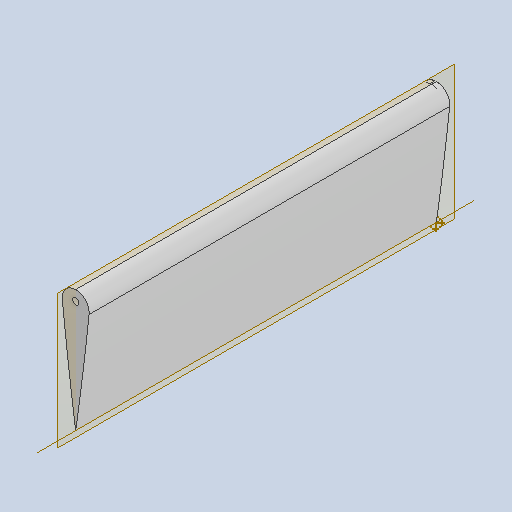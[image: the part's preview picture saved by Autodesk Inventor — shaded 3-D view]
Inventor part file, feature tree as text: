
AUTODESK INVENTOR PART (.ipt)
format: ipt  version: 2025.2 (Build 292293000, 293)  size: 148,480 bytes
history: native  units: in
note: dims shown in document units (in); Inventor stores cm internally (conversion verified against a paired STEP export)
features: other x5, sketch x1, plane x1
ambient origin geometry x8: Origin, YZ Plane, XZ Plane, XY Plane, X Axis, Y Axis, Z Axis, Center Point
bodies: Solid1 (feature_tree)
feature tree (7):
  other  "Elevator"
  other  "Solid1::Elevator"
  other  "TaggingFeature1"
  sketch  "Sketch3"  dims[d0=0.3937in]
  plane  "Work Plane1"
  other  "Work Axis1"
  other  "Work Point1"
